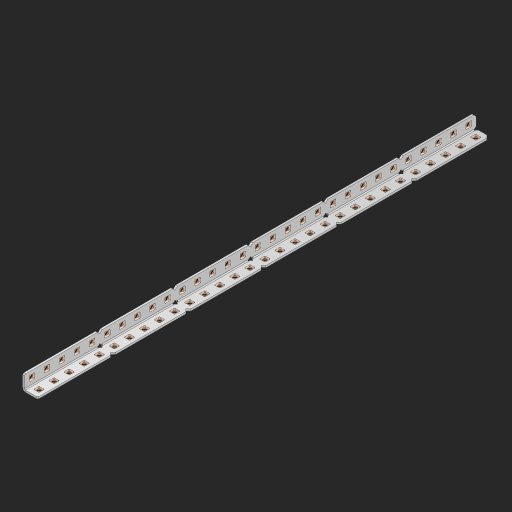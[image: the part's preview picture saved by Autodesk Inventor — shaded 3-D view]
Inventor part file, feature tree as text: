
AUTODESK INVENTOR PART (.ipt)
format: ipt  version: 2023 (Build 270158000, 158)  size: 1,034,752 bytes
history: native  units: in
note: dims shown in document units (in); Inventor stores cm internally (conversion verified against a paired STEP export)
features: other x66, extrude x61, sheet_metal_op x8, sketch x5, pattern_linear x1, mirror x1, chamfer x1
ambient origin geometry x8: Origin, YZ Plane, XZ Plane, XY Plane, X Axis, Y Axis, Z Axis, Center Point
bodies: Solid1 (feature_tree), Body (feature_tree)
feature tree (143):
  sheet_metal_op  "Flanges"
  sheet_metal_op  "Body Pattern"
  other  "Arc Length"
  pattern_linear  "Notch Pattern"  Spacing1=0.125in  [1 undecoded]
  other  "Diagonal Plane"
  mirror  "Everything Mirrored"
  chamfer  "End Chamfer"
  sketch  "Sketch1"  dims[d0=0.5in]
  other  "Plate1"
  sketch  "Sketch2"  dims[d1=15.0in]
  other  "Plate2"
  sheet_metal_op  "Bend1"
  sheet_metal_op  "Corner1"
  sketch  "Sketch8"  dims[d2=0.0625in]
  sketch  "Sketch9"  dims[d3=0.0625in]
  other  "Srf91"
  sheet_metal_op  "Body Pattern Sketch"
  other  "Srf92"
  sketch  "Sketch13"  dims[d4=0.0312in d5=0.125in d6=0.0625in d7=0.5in d8=90.0deg d9=0.0312in d10=0.25in d11=0.0625in d12=0.0625in d49=0.182in d50=0.02in d52=0.25in d53=0.0625in d54=0.0in d55=0.172in d56=1.0in d57=0.0in d85=0.1473in d86=0.1782in d89=0.0625in d90=0.0in d91=0.04in d92=0.0491in d95=2.5in d96=0.04in d97=0.25in d98=45.0deg d123=0.204in d126=0.0491in d127=0.1473in d128=0.08in d129=0.04in d130=2.5in d131=11.811in d133=0.5in d134=0.3937in d136=1.0in]
  other  "Srf856"
  other  "Srf857"
  other  "Srf858"
  other  "Srf859"
  other  "Srf860"
  other  "Srf861"
  other  "Srf1275"
  other  "Srf1276"
  other  "Srf1278"
  other  "Srf1279"
  other  "Srf1280"
  other  "Srf1281"
  other  "Srf1282"
  other  "Srf1283"
  other  "Srf1383"
  other  "Srf1384"
  other  "Srf1385"
  other  "Srf1386"
  other  "Srf1387"
  other  "Srf1388"
  other  "Srf1389"
  other  "Srf1390"
  other  "Srf1391"
  other  "Srf1392"
  other  "Srf1393"
  other  "Srf1394"
  other  "Srf1395"
  other  "Srf1396"
  other  "Srf1397"
  other  "Srf1398"
  other  "Srf1399"
  other  "Srf1400"
  other  "Srf1401"
  other  "Srf1402"
  other  "Srf1403"
  other  "Srf1404"
  other  "Srf1405"
  other  "Srf1475"
  other  "Srf1476"
  other  "Srf1477"
  other  "Srf1478"
  other  "Srf1479"
  other  "Srf1480"
  other  "Srf1481"
  other  "Srf1482"
  other  "Srf1483"
  other  "Srf1484"
  other  "Srf1485"
  other  "Srf1486"
  other  "Srf1487"
  other  "Srf1488"
  other  "Srf1489"
  other  "Srf1490"
  other  "Srf1491"
  other  "Srf1492"
  other  "Srf1493"
  other  "Srf1494"
  other  "Srf1495"
  other  "Srf1496"
  other  "Srf1497"
  sheet_metal_op  "Body Stamp"
  sheet_metal_op  "Body Circle"
  sheet_metal_op  "Notch"
  extrude  "ExtrusionSrf92"  Depth=0.0625in
  extrude  "ExtrusionSrf856"  Depth=0.5in TaperAngle=90.0deg
  extrude  "ExtrusionSrf857"  Depth=0.25in
  extrude  "ExtrusionSrf858"  Depth=0.0625in
  extrude  "ExtrusionSrf859"  Depth=0.0625in
  extrude  "ExtrusionSrf860"  Depth=0.3937in
  extrude  "ExtrusionSrf861"  Depth=0.02in
  extrude  "ExtrusionSrf1275"  Depth=0.25in
  extrude  "ExtrusionSrf1276"  Depth=0.0625in
  extrude  "ExtrusionSrf1277"  TaperAngle=0.0deg  [1 undecoded]
  extrude  "ExtrusionSrf1278"  Depth=0.3937in
  extrude  "ExtrusionSrf1279"  Depth=0.3937in TaperAngle=0.0deg
  extrude  "ExtrusionSrf1280"  Depth=0.3937in
  extrude  "ExtrusionSrf1281"  Depth=0.3937in
  extrude  "ExtrusionSrf1282"  Depth=0.0625in
  extrude  "ExtrusionSrf1383"  Depth=0.3937in TaperAngle=0.0deg
  extrude  "ExtrusionSrf1384"  Depth=0.3937in
  extrude  "ExtrusionSrf1385"  Depth=0.25in TaperAngle=45.0deg
  extrude  "ExtrusionSrf1386"  Depth=0.3937in
  extrude  "ExtrusionSrf1387"  Depth=0.3937in
  extrude  "ExtrusionSrf1388"  Depth=0.3937in
  extrude  "ExtrusionSrf1389"  Depth=0.3937in
  extrude  "ExtrusionSrf1390"  Depth=0.3937in
  extrude  "ExtrusionSrf1391"  Depth=0.3937in
  extrude  "ExtrusionSrf1392"  Depth=0.3937in
  extrude  "ExtrusionSrf1393"  Depth=0.5in
  extrude  "ExtrusionSrf1394"  [1 undecoded]
  extrude  "ExtrusionSrf1395"  [1 undecoded]
  extrude  "ExtrusionSrf1396"  [1 undecoded]
  extrude  "ExtrusionSrf1397"  [1 undecoded]
  extrude  "ExtrusionSrf1398"  [1 undecoded]
  extrude  "ExtrusionSrf1399"  [1 undecoded]
  extrude  "ExtrusionSrf1400"  [1 undecoded]
  extrude  "ExtrusionSrf1401"  [1 undecoded]
  extrude  "ExtrusionSrf1402"  [1 undecoded]
  extrude  "ExtrusionSrf1403"  [1 undecoded]
  extrude  "ExtrusionSrf1404"  [1 undecoded]
  extrude  "ExtrusionSrf1405"  [1 undecoded]
  extrude  "ExtrusionSrf1475"  [1 undecoded]
  extrude  "ExtrusionSrf1476"  [1 undecoded]
  extrude  "ExtrusionSrf1477"  [1 undecoded]
  extrude  "ExtrusionSrf1478"  [1 undecoded]
  extrude  "ExtrusionSrf1479"  [1 undecoded]
  extrude  "ExtrusionSrf1480"  [1 undecoded]
  extrude  "ExtrusionSrf1481"  [1 undecoded]
  extrude  "ExtrusionSrf1482"  [1 undecoded]
  extrude  "ExtrusionSrf1483"  [1 undecoded]
  extrude  "ExtrusionSrf1484"  [1 undecoded]
  extrude  "ExtrusionSrf1485"  [1 undecoded]
  extrude  "ExtrusionSrf1486"  [1 undecoded]
  extrude  "ExtrusionSrf1487"  [1 undecoded]
  extrude  "ExtrusionSrf1488"  [1 undecoded]
  extrude  "ExtrusionSrf1489"  [1 undecoded]
  extrude  "ExtrusionSrf1490"  [1 undecoded]
  extrude  "ExtrusionSrf1491"  [1 undecoded]
  extrude  "ExtrusionSrf1492"  [1 undecoded]
  extrude  "ExtrusionSrf1493"  [1 undecoded]
  extrude  "ExtrusionSrf1494"  [1 undecoded]
  extrude  "ExtrusionSrf1495"  [1 undecoded]
  extrude  "ExtrusionSrf1496"  [1 undecoded]
  extrude  "ExtrusionSrf1497"  [1 undecoded]
note: 37 required parameter values undecoded (feature->parameter linkage not recoverable at this tier; creation-order binding heuristic only, values carry confidence <= 0.55)
